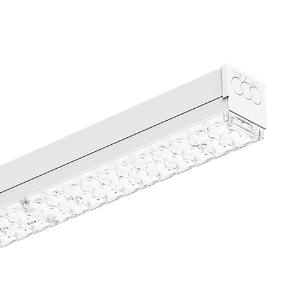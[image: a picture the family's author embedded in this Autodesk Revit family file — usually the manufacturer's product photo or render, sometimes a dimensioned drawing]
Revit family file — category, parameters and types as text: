
# Revit family: 3f_filippi_-_3f_zeta_l_3f_filippi_-_10892_-_3f_zeta_l_40_led_l1489
name_source: partatom
category: Lighting Fixtures
units: mm (PartAtom-declared; Revit-internal decimal feet)

## family parameters
Cut with Voids When Loaded = No
Host = Face
Light Source = No
Part Type = Normal
Room Calculation Point = No
Round Connector Dimension = Use Diameter
Shared = No

## types (1)
- 3F Filippi - 3F Zeta L (1 x LED, 6872 lm, 38.5 W, 4000 K)
    Apparent Load = 39 VA
    Approval mark = CE
    CIE Flux Codes = 61 95 99 99 100
    Color Rendering = 80
    Color Temperature = 4000 K
    Control Gear = Electronic ballast
    Default Elevation = 1800 mm
    Description = ILLUMINOTECHNICAL
Luminous efficiency 100% (DLOR 99%, ULOR 1%).
Initial luminous flux of the luminaire 6872 lm.
Direct symmetric distribution.
Installation Interdistance Transv.D = 1.39 x hu - Long.D = 1.43 x hu.
Tabular UGR (CIE 117 - 4H-8H; S=0.25H; 70/50/20): RUG 21.7 - 22.4.
Beam angle: 102° - 103°.
Luminous efficacy 178 lm/W.
Lifetime (L93/B10): 30000 h. (tq+25°C)
Lifetime (L90/B10): 50000 h. (tq+25°C)
Lifetime (L85/B10): 80000 h. (tq+25°C)
Lifetime (L80/B10): 100000 h. (tq+25°C)
Sudden decreased luminous flux after 50000 hours: 0% (C0).
Photobiological safety in compliance with IEC/TR 62778: RG0 risk exempt, (IEC 62471).
In compliance with IEC/EN 62722-2-1 - IEC/EN 62717 standards.

SOURCE
Linear LED module 40W/840.
Energy efficiency class (UE 2019/2020 - UE 2019/2015): C.
CIE 13.3 Colour rendering index: CRI >80 (R9 <50%).
IES TM-30 Fidelity Index: Rf = 84 Rg = 95.
CCT nominal colour temperature 4000 K.
Colour initial tolerance (MacAdam): SDCM 3.

MECHANICAL
Housing in hot-galvanised steel, painted in white polyester, obtained through rolling process.
Light unit in hot-galvanised steel, painted in white polyester base with fixing springs and retractable safety hooks in stainless steel.
Lenses for wide distribution, in transparent methacrylate (PMMA) with external flat surface.
End caps in white polycarbonate.
Pair of stainless steel sliding brackets with sliding block screws.
Luminaire with limited surface temperature. - D - (EN 60598-2-24)
Dimensions: 1489x62 mm, height 65 mm. Weight 3.35 kg.
IP40 protection degree.
Mechanical strength to impacts IK06 (1 joule).
Glow-wire test resistance 650°C.

ELECTRICAL
Halogen Free electronic wiring 230V-50/60Hz, power factor 0.95, THD <25%, constant output current, class I, 1 driver.
Power of the luminaire 38.5 W.
ENEC - CE.
SAFE FLICKER: PstLM=<1 and SVM=<0.4 (IEC TR 61547-1 and IEC TR 63158), to ensure a more comfortable and safe light.
Luminaire compliant with EN 60598-2-22 for power supply from a centralised emergency system CPSS (Central Power Supply System), not incorporated in the luminaire - high risk areas excluded. The default power and flux are 100% in AC and 100% in DC.
Ambient temperature from 0°C to +45°C.
Temperature class T6 max 85°C.
Relative humidity UR: <85%.

INSTALLATION
Ceiling / Suspended / Wall.
All accessories dedicated to this product are available on the Catalog and on our website www.3F-Filippi.com.

APPLICATIONS
Suitable product for food production plants (HACCP), IFS (Food Version 6), BRC (GSFS Food Version 7).
In commercial environments, exhibition areas, shops and stores.

WARNING
Luminaire designed for disposal/recycling at end-of-life.
Replaceable (LED only) light source by a professional. Replaceable control gear by a professional.
    Height = 65 mm
    Lamp = 1 x LED
    Lamp Light Flux = 6872 lm
    Lamp Power = 38.5 W
    Lamp count = 1
    Length = 1489 mm
    Lifetime = 50000 h
    Luminous efficacy = 178 lm/W
    Manufacturer = 3F Filippi
    ModVariant = No
    Model = 3F Filippi - 10892 - 3F Zeta L 40 LED L1489
    Mounting Place = Ceiling
    Mounting Type = Pendant
    Number of Poles = 1
    OnlyDefault = Yes
    Power Factor = 1
    Product Name = 3F Filippi - 3F Zeta L
    Product group = pendant luminaire
    ProductGroupID = 9
    Protection Class = Protection class I
    Protection Degree = IP 40
    RLX_Detail_Level = 1
    RLX_Emergency_Light_Flux = 0 lm
    RLX_Emergency_Type = 0
    RLX_Emergency_Type_DB = No
    RlxData = <blob elided: 37437 chars, md5=128628d2>
    Socket = socket
    Standby Power = 0 W
    System Light Flux = 6872 lm
    System Power = 39 W
    Type Comments = Product without accessories
    Type Image = 3ffilippi_3f_zeta_l.jpg
    URL = http://relux.com
    VarID = ---
    Voltage = 0 V
    Weight = 0.00 kg
    Width = 62 mm  [stored 0.203412 ft]

note: [stored X ft] marks values corroborated as IEEE doubles in the binary element streams (Revit-internal decimal feet)

## geometry (parser evidence)
native form markers: Blend x4, Sweep x12
no freeform markers — native parametric forms only
